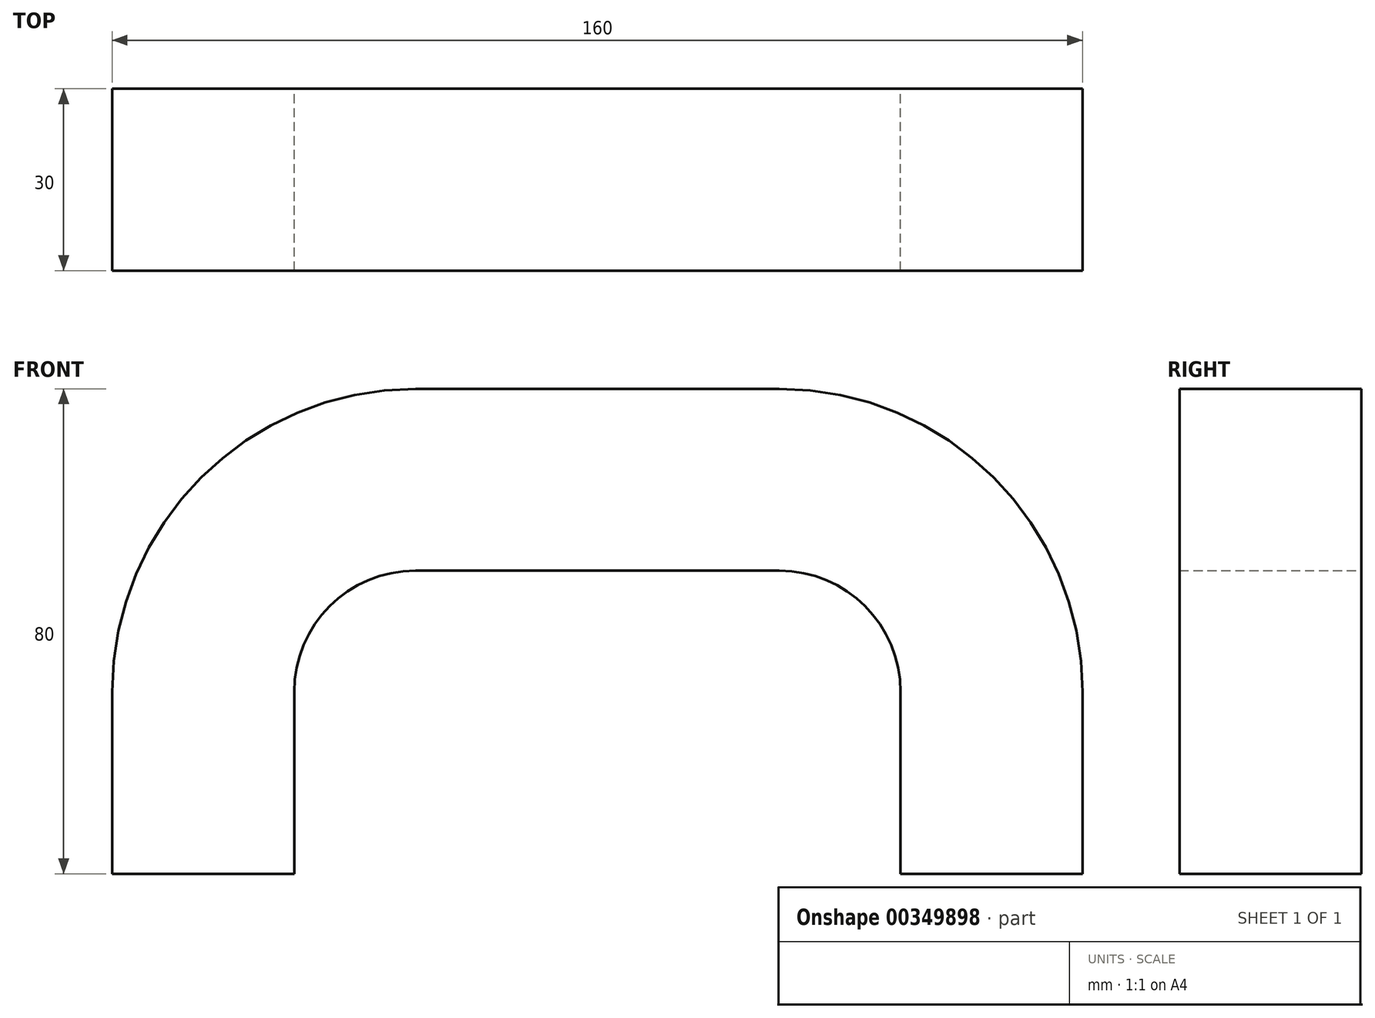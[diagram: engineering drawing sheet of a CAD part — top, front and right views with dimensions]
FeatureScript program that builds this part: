
annotation { "Feature Type Name" : "Feature", "Feature Type Description" : "" }
export const myFeature = defineFeature(function(context is Context, id is Id, definition is map)
    precondition{}
    {
        {
            var Q0;
            Q0=qCreatedBy(makeId("Front.planeOp"),FACE);
            var sketch = newSketch(context, id + "F0", { "sketchPlane" : qUnion([Q0])});
            skLineSegment(sketch, "E0.bottom", {"start": v(50, 0) * mm, "end": v(110, 0) * mm});
            skLineSegment(sketch, "E0.top", {"start": v(0, -80) * mm, "end": v(30, -80) * mm});
            skLineSegment(sketch, "E0.left", {"start": v(0, -50) * mm, "end": v(0, -80) * mm});
            skLineSegment(sketch, "E0.right", {"start": v(160, -50) * mm, "end": v(160, -80) * mm});
            skPoint(sketch, "E1.visualSharp", {"position": v(0, 0) * mm});
            skArc(sketch, "E1.filletArc", {"start": v(50, 0) * mm, "mid": v(14.64, -14.64) * mm, "end": v(0, -50) * mm});
            skPoint(sketch, "E2.visualSharp", {"position": v(160, 0) * mm});
            skArc(sketch, "E2.filletArc", {"start": v(160, -50) * mm, "mid": v(145.36, -14.64) * mm, "end": v(110, 0) * mm});
            skLineSegment(sketch, "E3.0", {"start": v(130, -50) * mm, "end": v(130, -80) * mm});
            skLineSegment(sketch, "E3.1", {"start": v(30, -50) * mm, "end": v(30, -80) * mm});
            skArc(sketch, "E3.2", {"start": v(50, -30) * mm, "mid": v(35.86, -35.86) * mm, "end": v(30, -50) * mm});
            skLineSegment(sketch, "E3.3", {"start": v(50, -30) * mm, "end": v(110, -30) * mm});
            skArc(sketch, "E3.4", {"start": v(130, -50) * mm, "mid": v(124.14, -35.86) * mm, "end": v(110, -30) * mm});
            skLineSegment(sketch, "E4.trimOffspring", {"start": v(130, -80) * mm, "end": v(160, -80) * mm});
            skSolve(sketch);
        }
        {
            var Q0;
            Q0 = qSketchRegion(id + "F0", true);
            extrude(context, id + "F1", {"entities" : qUnion([Q0]), "depth" : 30 * mm});
        }
    });
